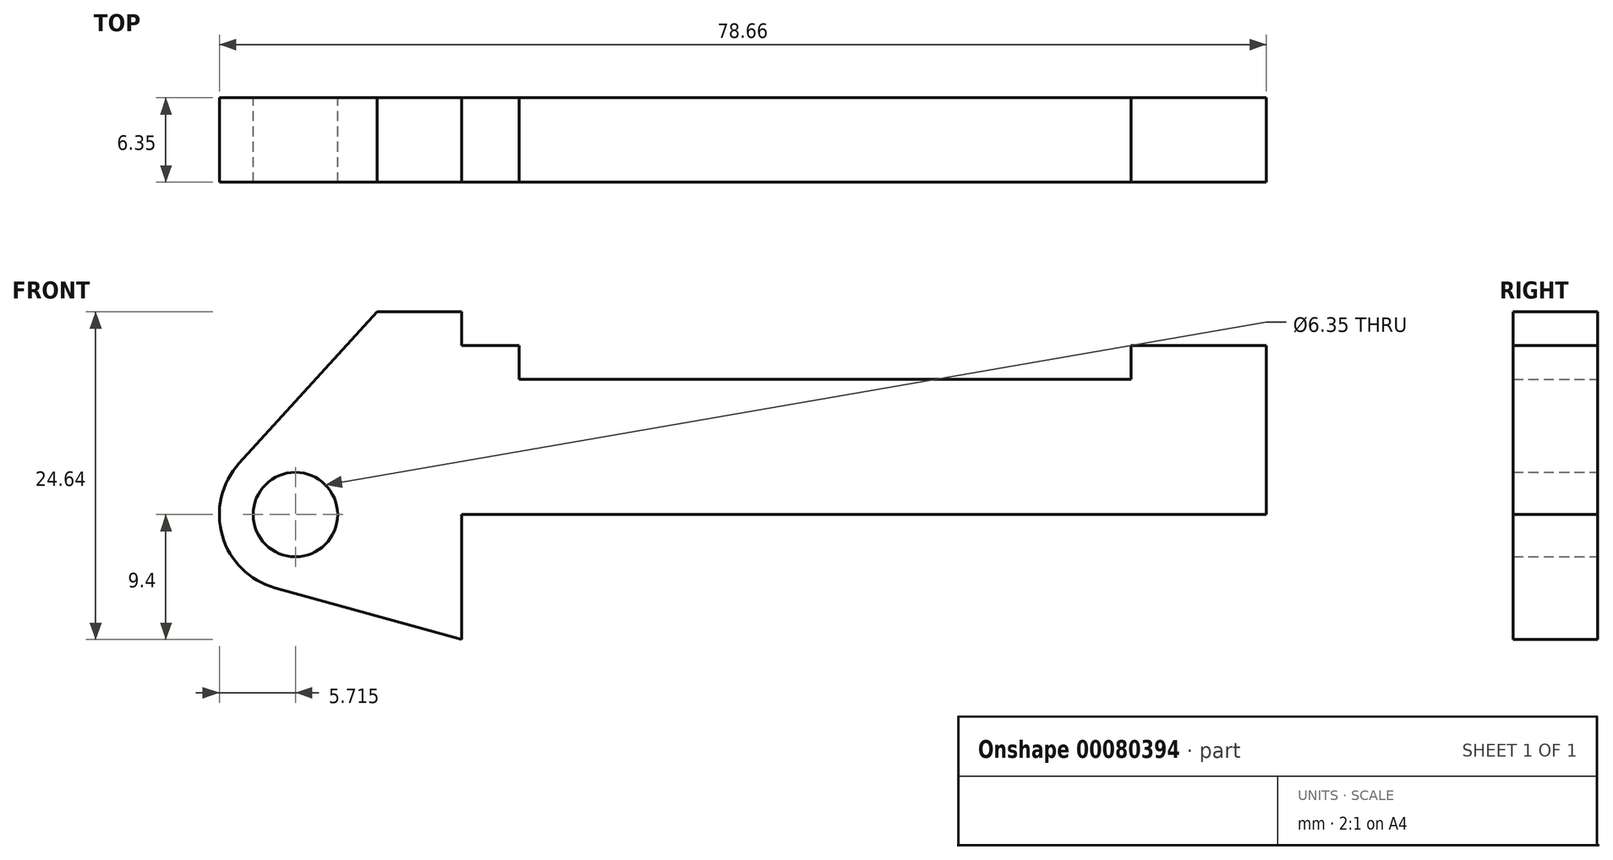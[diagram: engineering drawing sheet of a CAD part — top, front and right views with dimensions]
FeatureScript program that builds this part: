
annotation { "Feature Type Name" : "Feature", "Feature Type Description" : "" }
export const myFeature = defineFeature(function(context is Context, id is Id, definition is map)
    precondition{}
    {
        {
            var Q0;
            Q0=qCreatedBy(makeId("Front.planeOp"),FACE);
            var sketch = newSketch(context, id + "F0", { "sketchPlane" : qUnion([Q0])});
            skLineSegment(sketch, "E0", {"start": v(0, 0) * mm, "end": v(0, 12.7) * mm});
            skLineSegment(sketch, "E1", {"start": v(0, 12.7) * mm, "end": v(10.16, 12.7) * mm});
            skLineSegment(sketch, "E2", {"start": v(10.16, 12.7) * mm, "end": v(10.16, 10.16) * mm});
            skLineSegment(sketch, "E3", {"start": v(10.16, 10.16) * mm, "end": v(56.13, 10.16) * mm});
            skLineSegment(sketch, "E4", {"start": v(56.13, 10.16) * mm, "end": v(56.13, 12.7) * mm});
            skLineSegment(sketch, "E5", {"start": v(56.13, 12.7) * mm, "end": v(66.3, 12.7) * mm});
            skLineSegment(sketch, "E6", {"start": v(66.3, 12.7) * mm, "end": v(66.3, 0) * mm});
            skLineSegment(sketch, "E7", {"start": v(66.3, 0) * mm, "end": v(0, 0) * mm});
            skLineSegment(sketch, "E8", {"start": v(5.84, 15.24) * mm, "end": v(-0.5, 15.24) * mm});
            skLineSegment(sketch, "E9", {"start": v(-0.5, 15.24) * mm, "end": v(-10.88, 3.85) * mm});
            skLineSegment(sketch, "E10", {"start": v(0, 0) * mm, "end": v(-6.65, 0) * mm});
            skCircle(sketch, "E11", {"center": v(-6.65, 0) * mm, "radius": 5.72 * mm});
            skCircle(sketch, "E12", {"center": v(-6.65, 0) * mm, "radius": 3.18 * mm});
            skLineSegment(sketch, "E13", {"start": v(5.84, 15.24) * mm, "end": v(5.84, -9.4) * mm});
            skLineSegment(sketch, "E14", {"start": v(5.84, -9.4) * mm, "end": v(-8.18, -5.5) * mm});
            skSolve(sketch);
        }
        {
            var Q0;
            Q0 = qSketchRegion(id + "F0", true);
            extrude(context, id + "F1", {"entities" : qUnion([Q0]), "depth" : 6.35 * mm});
        }
    });
